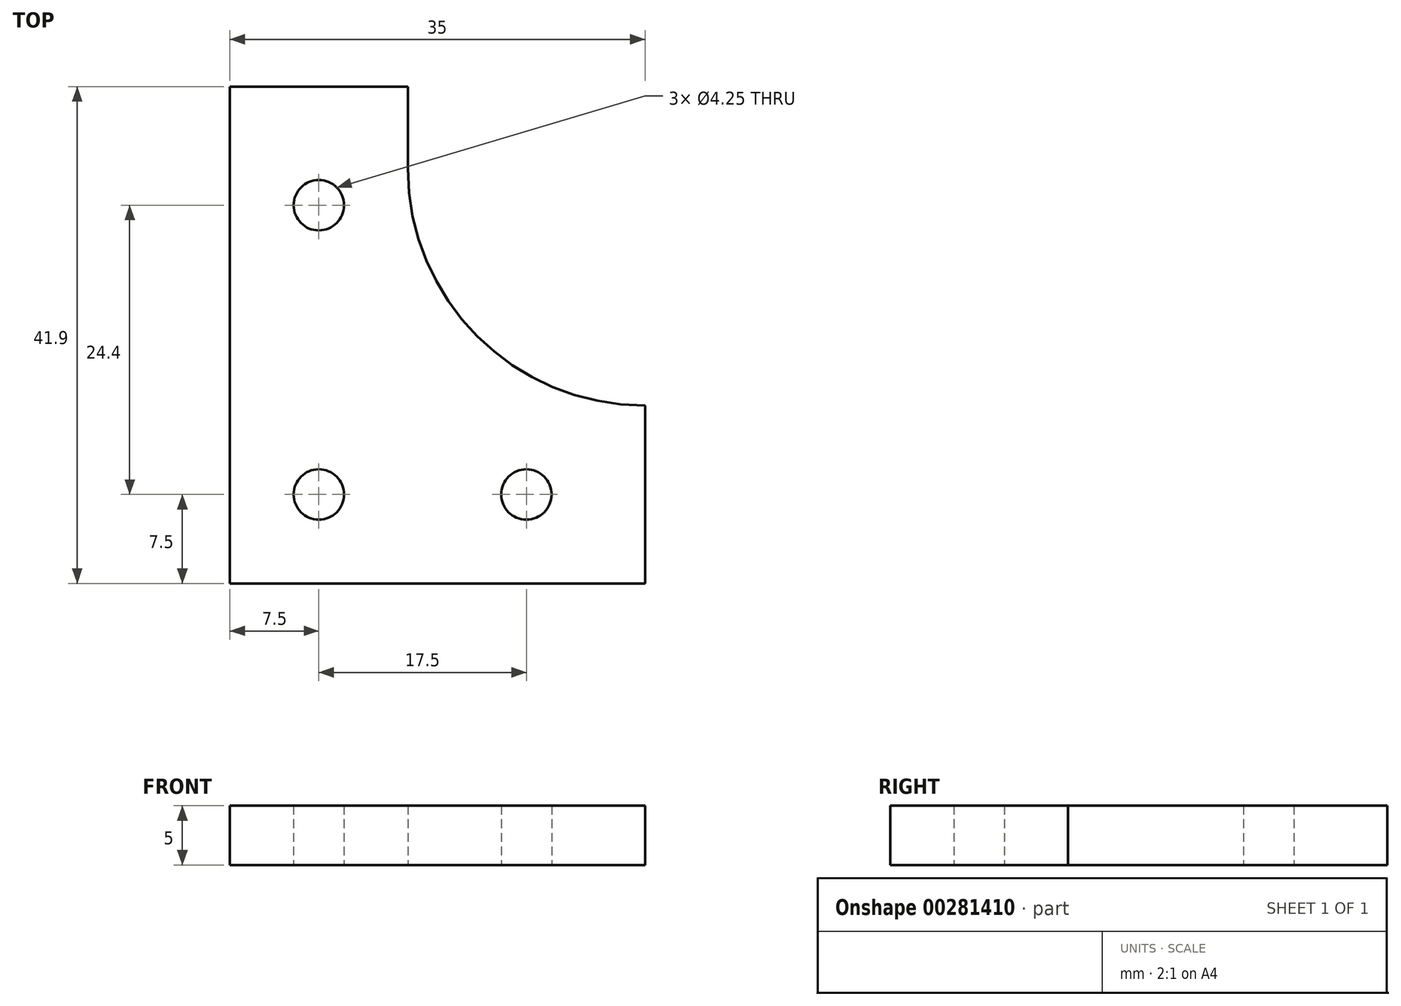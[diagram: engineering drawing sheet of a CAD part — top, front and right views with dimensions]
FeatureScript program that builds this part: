
annotation { "Feature Type Name" : "Feature", "Feature Type Description" : "" }
export const myFeature = defineFeature(function(context is Context, id is Id, definition is map)
    precondition{}
    {
        {
            var Q0;
            Q0=qCreatedBy(makeId("Top.planeOp"),FACE);
            var sketch = newSketch(context, id + "F0", { "sketchPlane" : qUnion([Q0])});
            skLineSegment(sketch, "E0", {"start": v(-15, 26.9) * mm, "end": v(-15, -15) * mm});
            skLineSegment(sketch, "E1", {"start": v(-15, -15) * mm, "end": v(20, -15) * mm});
            skLineSegment(sketch, "E2", {"start": v(20, -15) * mm, "end": v(20, 0) * mm});
            skLineSegment(sketch, "E3", {"start": v(20, 0) * mm, "end": v(20, 0) * mm});
            skLineSegment(sketch, "E4", {"start": v(0, 20) * mm, "end": v(0, 26.9) * mm});
            skLineSegment(sketch, "E5", {"start": v(0, 26.9) * mm, "end": v(-15, 26.9) * mm});
            skPoint(sketch, "E6.visualSharp", {"position": v(0, 0) * mm});
            skArc(sketch, "E6.filletArc", {"start": v(0, 20) * mm, "mid": v(5.86, 5.86) * mm, "end": v(20, 0) * mm});
            skCircle(sketch, "E7", {"center": v(-7.5, 16.9) * mm, "radius": 2.12 * mm});
            skCircle(sketch, "E8", {"center": v(10, -7.5) * mm, "radius": 2.12 * mm});
            skCircle(sketch, "E9", {"center": v(-7.5, -7.5) * mm, "radius": 2.12 * mm});
            skSolve(sketch);
        }
        {
            var Q0;
            Q0=qSketchRegion(id+"F0",true);
            extrude(context, id + "F1", {"entities" : qUnion([Q0]), "depth" : 5 * mm});
        }
    });
